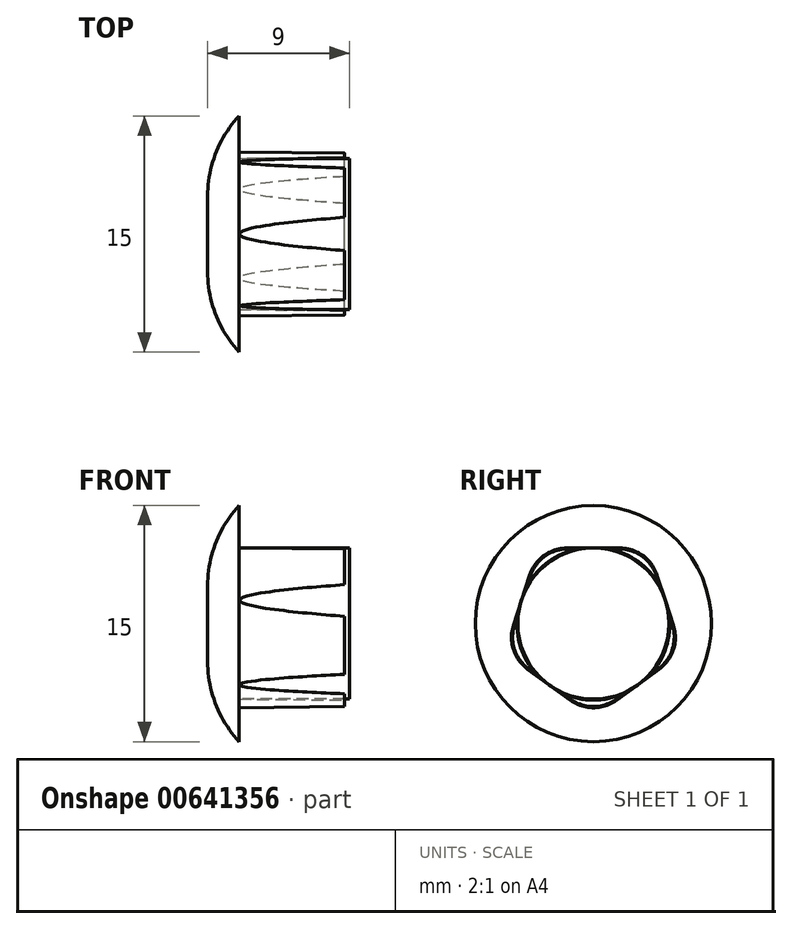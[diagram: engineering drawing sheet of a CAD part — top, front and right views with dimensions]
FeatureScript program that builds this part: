
annotation { "Feature Type Name" : "Feature", "Feature Type Description" : "" }
export const myFeature = defineFeature(function(context is Context, id is Id, definition is map)
    precondition{}
    {
        {
            var Q0;
            Q0=qCreatedBy(makeId("Right.planeOp"),FACE);
            var sketch = newSketch(context, id + "F0", { "sketchPlane" : qUnion([Q0])});
            skCircle(sketch, "E0", {"center": v(0, 0) * mm, "radius": 7.5 * mm});
            skCircle(sketch, "E1", {"center": v(0, 0) * mm, "radius": 4.8 * mm});
            skCircle(sketch, "E2.cCircle", {"center": v(0, 0) * mm, "radius": 4.8 * mm, "construction": true});
            skLineSegment(sketch, "E2.0", {"start": v(-3.49, 4.8) * mm, "end": v(3.49, 4.8) * mm});
            skLineSegment(sketch, "E2.1", {"start": v(3.49, 4.8) * mm, "end": v(5.64, -1.83) * mm});
            skLineSegment(sketch, "E2.2", {"start": v(5.64, -1.83) * mm, "end": v(0, -5.93) * mm});
            skLineSegment(sketch, "E2.3", {"start": v(0, -5.93) * mm, "end": v(-5.64, -1.83) * mm});
            skLineSegment(sketch, "E2.4", {"start": v(-5.64, -1.83) * mm, "end": v(-3.49, 4.8) * mm});
            skPoint(sketch, "E2.0.midPoint", {"position": v(0, 4.8) * mm});
            skSolve(sketch);
        }
        {
            var Q0;
            {var subQ0=sQuery(id+"F0.wireOp",EDGE,"E1");var subQ4=makeQuery(id+"F0.imprint","INTERSECT",VERTEX,{"derivedFrom":[subQ0,sQuery(id+"F0.wireOp",EDGE,"E2.0")]});Q0=makeQuery(id+"F0.imprint","IMPRINT",FACE,{"disambiguationData":[TD([[makeQuery(id+"F0.imprint","IMPRINT",EDGE,{"disambiguationData":[TD([[subQ4,1.0]])],"derivedFrom":subQ0}),1.0]])]});}
            extrude(context, id + "F1", {"entities" : qUnion([Q0]), "depth" : 7 * mm, "offsetDistance" : 25 * mm});
        }
        {
            var Q0;
            {var subQ0=sQuery(id+"F0.wireOp",EDGE,"E2.4");var subQ1=sQuery(id+"F0.wireOp",EDGE,"E1");var subQ2=makeQuery(id+"F0.imprint","INTERSECT",VERTEX,{"derivedFrom":[subQ1,subQ0]});Q0=makeQuery(id+"F0.imprint","IMPRINT",FACE,{"disambiguationData":[TD([[makeQuery(id+"F0.imprint","IMPRINT",EDGE,{"disambiguationData":[TD([[subQ2,-1.0]])],"derivedFrom":subQ1}),-1.0]])]});}
            var Q1;
            {var subQ0=sQuery(id+"F0.wireOp",EDGE,"E1");var subQ4=makeQuery(id+"F0.imprint","INTERSECT",VERTEX,{"derivedFrom":[subQ0,sQuery(id+"F0.wireOp",EDGE,"E2.0")]});Q1=makeQuery(id+"F0.imprint","IMPRINT",FACE,{"disambiguationData":[TD([[makeQuery(id+"F0.imprint","IMPRINT",EDGE,{"disambiguationData":[TD([[subQ4,1.0]])],"derivedFrom":subQ0}),1.0]])]});}
            var Q2;
            {var subQ0=sQuery(id+"F0.wireOp",EDGE,"E2.0");var subQ1=sQuery(id+"F0.wireOp",EDGE,"E1");var subQ2=makeQuery(id+"F0.imprint","INTERSECT",VERTEX,{"derivedFrom":[subQ1,subQ0]});Q2=makeQuery(id+"F0.imprint","IMPRINT",FACE,{"disambiguationData":[TD([[makeQuery(id+"F0.imprint","IMPRINT",EDGE,{"disambiguationData":[TD([[subQ2,-1.0]])],"derivedFrom":subQ1}),-1.0]])]});}
            var Q3;
            {var subQ0=sQuery(id+"F0.wireOp",EDGE,"E2.0");var subQ1=sQuery(id+"F0.wireOp",EDGE,"E1");var subQ2=makeQuery(id+"F0.imprint","INTERSECT",VERTEX,{"derivedFrom":[subQ1,subQ0]});Q3=makeQuery(id+"F0.imprint","IMPRINT",FACE,{"disambiguationData":[TD([[makeQuery(id+"F0.imprint","IMPRINT",EDGE,{"disambiguationData":[TD([[subQ2,1.0]])],"derivedFrom":subQ1}),-1.0]])]});}
            var Q4;
            {var subQ0=sQuery(id+"F0.wireOp",EDGE,"E2.1");var subQ1=sQuery(id+"F0.wireOp",EDGE,"E1");var subQ2=makeQuery(id+"F0.imprint","INTERSECT",VERTEX,{"derivedFrom":[subQ1,subQ0]});Q4=makeQuery(id+"F0.imprint","IMPRINT",FACE,{"disambiguationData":[TD([[makeQuery(id+"F0.imprint","IMPRINT",EDGE,{"disambiguationData":[TD([[subQ2,1.0]])],"derivedFrom":subQ1}),-1.0]])]});}
            var Q5;
            {var subQ0=sQuery(id+"F0.wireOp",EDGE,"E2.3");var subQ1=sQuery(id+"F0.wireOp",EDGE,"E1");var subQ2=makeQuery(id+"F0.imprint","INTERSECT",VERTEX,{"derivedFrom":[subQ1,subQ0]});Q5=makeQuery(id+"F0.imprint","IMPRINT",FACE,{"disambiguationData":[TD([[makeQuery(id+"F0.imprint","IMPRINT",EDGE,{"disambiguationData":[TD([[subQ2,-1.0]])],"derivedFrom":subQ1}),-1.0]])]});}
            var Q6;
            Q6=makeQuery(id+"F0.imprint","IMPRINT",FACE,{"disambiguationData":[TD([[makeQuery(id+"F0.imprint","IMPRINT",EDGE,{"derivedFrom":sQuery(id+"F0.wireOp",EDGE,"E0")}),1.0]])]});
            extrude(context, id + "F2", {"entities" : qUnion([Q0, Q1, Q2, Q3, Q4, Q5, Q6]), "operationType" : NewBodyOperationType.ADD, "oppositeDirection" : true, "depth" : 2 * mm, "offsetDistance" : 25 * mm});
        }
        {
            var Q0;
            Q0=makeQuery(id+"F2.opExtrude","CAP_EDGE",EDGE,{"disambiguationData":[OSD([sQuery(id+"F0.wireOp",EDGE,"E0")])],"isStart":false});
            fillet(context, id + "F3", {"entities" : qUnion([Q0]), "radius" : 7.5 * mm, "tangentPropagation" : true, "allowEdgeOverflow" : false});
        }
        {
            var Q0;
            {var subQ0=sQuery(id+"F0.wireOp",EDGE,"E2.0");var subQ1=sQuery(id+"F0.wireOp",EDGE,"E1");var subQ2=makeQuery(id+"F0.imprint","INTERSECT",VERTEX,{"derivedFrom":[subQ1,subQ0]});Q0=makeQuery(id+"F0.imprint","IMPRINT",FACE,{"disambiguationData":[TD([[makeQuery(id+"F0.imprint","IMPRINT",EDGE,{"disambiguationData":[TD([[subQ2,1.0]])],"derivedFrom":subQ1}),-1.0]])]});}
            var Q1;
            {var subQ0=sQuery(id+"F0.wireOp",EDGE,"E2.1");var subQ1=sQuery(id+"F0.wireOp",EDGE,"E1");var subQ2=makeQuery(id+"F0.imprint","INTERSECT",VERTEX,{"derivedFrom":[subQ1,subQ0]});Q1=makeQuery(id+"F0.imprint","IMPRINT",FACE,{"disambiguationData":[TD([[makeQuery(id+"F0.imprint","IMPRINT",EDGE,{"disambiguationData":[TD([[subQ2,1.0]])],"derivedFrom":subQ1}),-1.0]])]});}
            var Q2;
            {var subQ0=sQuery(id+"F0.wireOp",EDGE,"E2.3");var subQ1=sQuery(id+"F0.wireOp",EDGE,"E1");var subQ2=makeQuery(id+"F0.imprint","INTERSECT",VERTEX,{"derivedFrom":[subQ1,subQ0]});Q2=makeQuery(id+"F0.imprint","IMPRINT",FACE,{"disambiguationData":[TD([[makeQuery(id+"F0.imprint","IMPRINT",EDGE,{"disambiguationData":[TD([[subQ2,-1.0]])],"derivedFrom":subQ1}),-1.0]])]});}
            var Q3;
            {var subQ0=sQuery(id+"F0.wireOp",EDGE,"E2.0");var subQ1=sQuery(id+"F0.wireOp",EDGE,"E1");var subQ2=makeQuery(id+"F0.imprint","INTERSECT",VERTEX,{"derivedFrom":[subQ1,subQ0]});Q3=makeQuery(id+"F0.imprint","IMPRINT",FACE,{"disambiguationData":[TD([[makeQuery(id+"F0.imprint","IMPRINT",EDGE,{"disambiguationData":[TD([[subQ2,-1.0]])],"derivedFrom":subQ1}),-1.0]])]});}
            var Q4;
            {var subQ0=sQuery(id+"F0.wireOp",EDGE,"E2.4");var subQ1=sQuery(id+"F0.wireOp",EDGE,"E1");var subQ2=makeQuery(id+"F0.imprint","INTERSECT",VERTEX,{"derivedFrom":[subQ1,subQ0]});Q4=makeQuery(id+"F0.imprint","IMPRINT",FACE,{"disambiguationData":[TD([[makeQuery(id+"F0.imprint","IMPRINT",EDGE,{"disambiguationData":[TD([[subQ2,-1.0]])],"derivedFrom":subQ1}),-1.0]])]});}
            extrude(context, id + "F4", {"entities" : qUnion([Q0, Q1, Q2, Q3, Q4]), "operationType" : NewBodyOperationType.ADD, "depth" : 6.7 * mm, "offsetDistance" : 25 * mm, "hasDraft" : true, "draftAngle" : 0.5 * degree, "draftPullDirection" : true});
        }
        {
            var Q0;
            Q0=makeQuery(id+"F4.opExtrude","SWEPT_EDGE",EDGE,{"disambiguationData":[OSD([sQuery(id+"F0.wireOp",EDGE,"E2.2"),sQuery(id+"F0.wireOp",EDGE,"E2.3")])]});
            var Q1;
            Q1=makeQuery(id+"F4.opExtrude","SWEPT_EDGE",EDGE,{"disambiguationData":[OSD([sQuery(id+"F0.wireOp",EDGE,"E2.3"),sQuery(id+"F0.wireOp",EDGE,"E2.4")])]});
            var Q2;
            Q2=makeQuery(id+"F4.opExtrude","SWEPT_EDGE",EDGE,{"disambiguationData":[OSD([sQuery(id+"F0.wireOp",EDGE,"E2.0"),sQuery(id+"F0.wireOp",EDGE,"E2.4")])]});
            var Q3;
            Q3=makeQuery(id+"F4.opExtrude","SWEPT_EDGE",EDGE,{"disambiguationData":[OSD([sQuery(id+"F0.wireOp",EDGE,"E2.0"),sQuery(id+"F0.wireOp",EDGE,"E2.1")])]});
            var Q4;
            Q4=makeQuery(id+"F4.opExtrude","SWEPT_EDGE",EDGE,{"disambiguationData":[OSD([sQuery(id+"F0.wireOp",EDGE,"E2.1"),sQuery(id+"F0.wireOp",EDGE,"E2.2")])]});
            fillet(context, id + "F5", {"entities" : qUnion([Q0, Q1, Q2, Q3, Q4]), "radius" : 2.5 * mm, "tangentPropagation" : true, "allowEdgeOverflow" : false});
        }
    });
